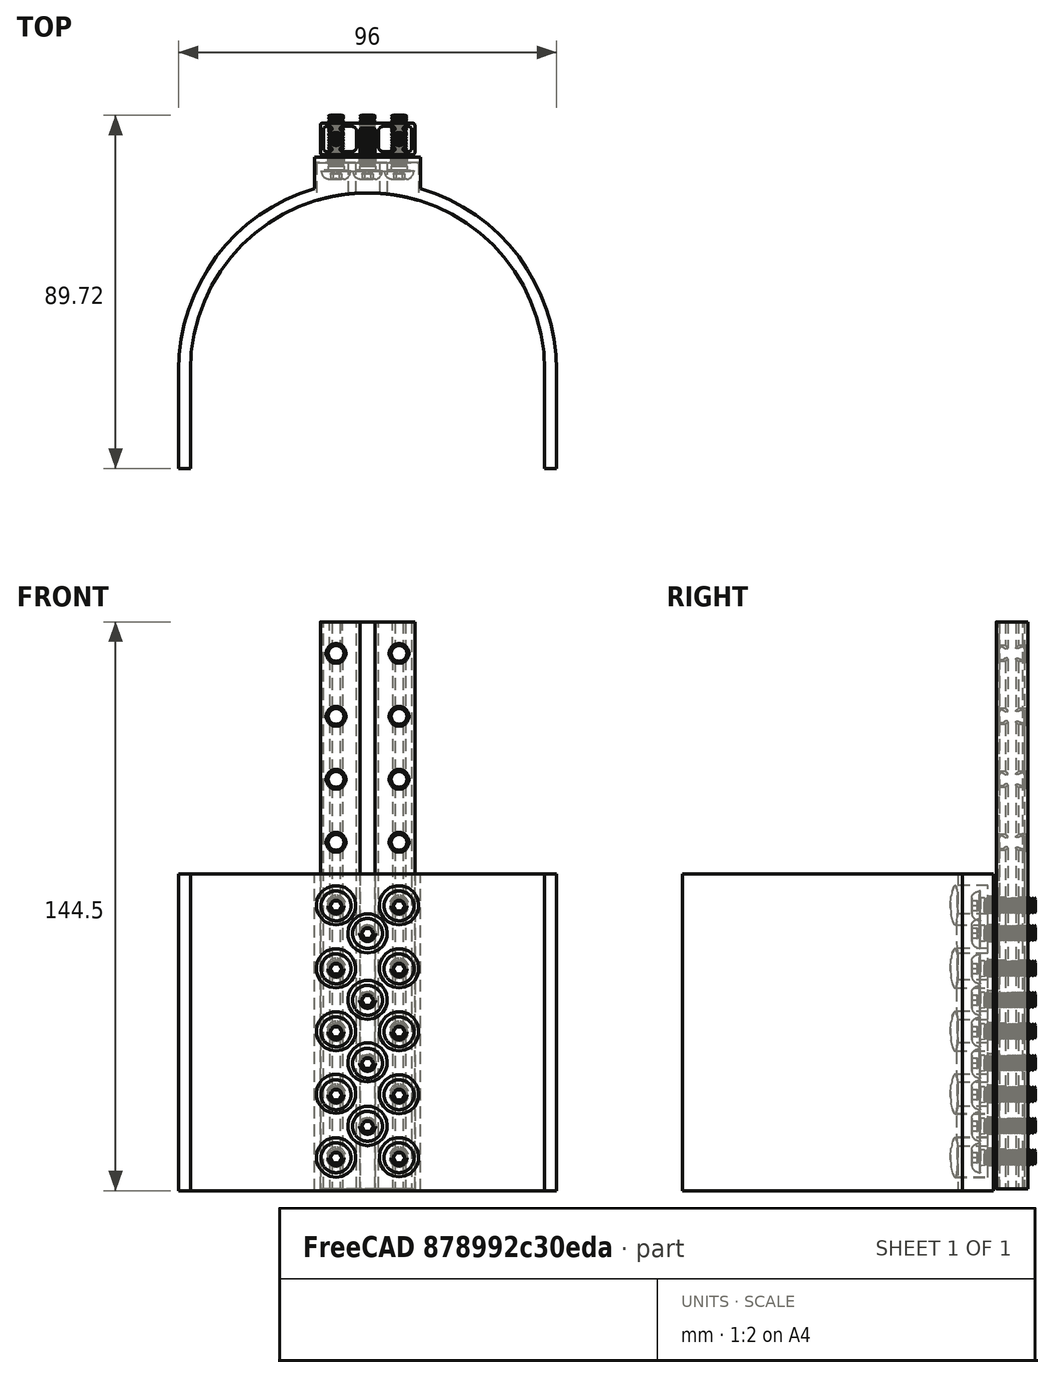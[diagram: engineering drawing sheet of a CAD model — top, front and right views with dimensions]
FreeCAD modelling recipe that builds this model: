
FCSTD DOCUMENT  (FreeCAD 0.21R33675 (Git))
Label: Mx 20223 Feeder Support v2
License: All rights reserved
LicenseURL: http://en.wikipedia.org/wiki/All_rights_reserved
objects: Part::Feature×15, Sketcher::SketchObject×3, PartDesign::Pocket×2, PartDesign::Pad×1, Mesh::Feature×1, PartDesign::Plane×1, PartDesign::Body×1
note: 26 computed .brp shape members not serialized (recipe doc carries the construction recipe); baked Part::Feature solids carry a one-line shape summary decoded from their .brp

FEATURE [Sketcher::SketchObject] Sketch
  FullyConstrained = false
  MapMode = 5
  Support = -> [XY_Plane]
  sketch-geometry (12):
    g0: LineSegment StartX=2.9811e-08 StartY=25.2897 StartZ=0 EndX=2.9811e-08 EndY=0.289669 EndZ=0
    g1: LineSegment StartX=96 StartY=25.2897 StartZ=0 EndX=96 EndY=0.289669 EndZ=0
    g2: ArcOfCircle CenterX=48 CenterY=25.2897 CenterZ=0 NormalX=0 NormalY=0 NormalZ=1 AngleXU=0 Radius=45 StartAngle=1e-16 EndAngle=3.14159
    g3: LineSegment StartX=2.9811e-08 StartY=0.289669 StartZ=0 EndX=3 EndY=0.289669 EndZ=0
    g4: LineSegment StartX=96 StartY=0.289669 StartZ=0 EndX=93 EndY=0.289669 EndZ=0
    g5: LineSegment StartX=93 StartY=25.2897 StartZ=0 EndX=93 EndY=0.289669 EndZ=0
    g6: LineSegment StartX=3 StartY=0.289669 StartZ=0 EndX=3 EndY=25.2897 EndZ=0
    g7: LineSegment StartX=34.5 StartY=79.3521 StartZ=0 EndX=61.5 EndY=79.3521 EndZ=0
    g8: LineSegment StartX=34.5 StartY=79.3521 StartZ=0 EndX=34.5 EndY=71.3521 EndZ=0
    g9: LineSegment StartX=61.5 StartY=79.3521 StartZ=0 EndX=61.5 EndY=71.3521 EndZ=0
    g10: ArcOfCircle CenterX=48 CenterY=25.2897 CenterZ=0 NormalX=0 NormalY=0 NormalZ=1 AngleXU=0 Radius=48 StartAngle=2e-16 EndAngle=1.2857
    g11: ArcOfCircle CenterX=48 CenterY=25.2897 CenterZ=0 NormalX=0 NormalY=0 NormalZ=1 AngleXU=0 Radius=48 StartAngle=1.85589 EndAngle=3.14159
  constraints (35):
    c: Vertical(g0)
    c: Vertical(g1)
    c: Equal(g0,g1)
    c: Angle(g2) = 3.14159
    c: Coincident(g3,g0)
    c: Horizontal(g3)
    c: Coincident(g4,g1)
    c: Equal(g3,g4)
    c: DistanceX(g3,g3) = 3
    c: Angle(g4,g1,g1) = 1.5708
    c: Coincident(g5,g2)
    c: Coincident(g5,g4)
    c: Coincident(g6,g3)
    c: Coincident(g6,g2)
    c: Vertical(g6)
    c: Diameter(g2) = 90
    c: DistanceY(g6,g6) = 25
    c: Equal(g6,g5)
    c: DistanceY(g0,g0) = 25
    c: Angle(g4,g5) = 1.5708
    c: DistanceY(g3,g4) = 0
    c: Horizontal(g7)
    c: DistanceX(g7,g7) = 27
    c: Coincident(g8,g7)
    c: Vertical(g8)
    c: Coincident(g9,g7)
    c: Vertical(g9)
    c: Coincident(g10,g2)
    c: Coincident(g10,g1)
    c: Coincident(g10,g9)
    c: Coincident(g11,g2)
    c: Coincident(g11,g8)
    c: Coincident(g11,g0)
    c: Equal(g8,g9)
    c: DistanceY(g8,g8) = 8
FEATURE [PartDesign::Pad] Pad
  Direction = (0,0,1)
  Length = 80.5
  Length2 = 10
  Profile = -> Sketch
  ReferenceAxis = -> Sketch [N_Axis]
  Type = 0
FEATURE [Mesh::Feature] Fantastic_Jaagub  label="ball"
  Placement = pos=(39,63,0) rot=(0,0,1;0rad)
FEATURE [Part::Feature] Part__Feature  label="Hexagon socket button head screws M4 001"
  Placement = pos=(56,90,24.5) rot=(0.01,0,0.99995;1.5708rad)
  shape: bbox 8.227 x 16.25 x 15.28 mm, 101 faces (baked)
FEATURE [Part::Feature] Part__Feature001  label="Beam0824-144˫¿؁º"
  Placement = pos=(48,88,0.5) rot=(0,0,1;3.14159rad)
  shape: bbox 24 x 8 x 144 mm, 662 faces (baked)
FEATURE [PartDesign::Plane] DatumPlane
  AttachmentOffset = pos=(0,0,14) rot=(0,1,0;3.14159rad)
  Length = 128.097
  MapMode = 45
  Placement = pos=(48,67.9376,40.25) rot=(0.57735,0.57735,-0.57735;2.0944rad)
  ResizeMode = 0
  Support = -> [Pad]
  Width = 143.597
FEATURE [Sketcher::SketchObject] Sketch001
  FullyConstrained = false
  MapMode = 5
  Placement = pos=(48,67.9376,40.25) rot=(-0.57735,-0.57735,0.57735;4.18879rad)
  Support = -> [DatumPlane]
  sketch-geometry (14):
    g0: Circle CenterX=31.8116 CenterY=-8.00605 CenterZ=0 NormalX=0 NormalY=0 NormalZ=1 AngleXU=0 Radius=5
    g1: Circle CenterX=31.7489 CenterY=7.99158 CenterZ=0 NormalX=0 NormalY=0 NormalZ=1 AngleXU=0 Radius=5
    g2: Circle CenterX=15.7464 CenterY=8.00103 CenterZ=0 NormalX=0 NormalY=0 NormalZ=1 AngleXU=0 Radius=5
    g3: Circle CenterX=15.6675 CenterY=-7.999 CenterZ=0 NormalX=0 NormalY=0 NormalZ=1 AngleXU=0 Radius=5
    g4: Circle CenterX=-0.253769 CenterY=-7.99844 CenterZ=0 NormalX=0 NormalY=0 NormalZ=1 AngleXU=0 Radius=5
    g5: Circle CenterX=-0.252174 CenterY=8.00175 CenterZ=0 NormalX=0 NormalY=0 NormalZ=1 AngleXU=0 Radius=5
    g6: Circle CenterX=-16.2562 CenterY=8.00301 CenterZ=0 NormalX=0 NormalY=0 NormalZ=1 AngleXU=0 Radius=5
    g7: Circle CenterX=-16.2572 CenterY=-8.02127 CenterZ=0 NormalX=0 NormalY=0 NormalZ=1 AngleXU=0 Radius=5
    g8: Circle CenterX=-32.2753 CenterY=-7.99234 CenterZ=0 NormalX=0 NormalY=0 NormalZ=1 AngleXU=0 Radius=5
    g9: Circle CenterX=-32.2552 CenterY=7.99149 CenterZ=0 NormalX=0 NormalY=0 NormalZ=1 AngleXU=0 Radius=5
    g10: Circle CenterX=-25.0915 CenterY=0 CenterZ=0 NormalX=0 NormalY=0 NormalZ=1 AngleXU=0 Radius=5
    g11: Circle CenterX=-8.28187 CenterY=0 CenterZ=0 NormalX=0 NormalY=0 NormalZ=1 AngleXU=0 Radius=5
    g12: Circle CenterX=7.66746 CenterY=0 CenterZ=0 NormalX=0 NormalY=0 NormalZ=1 AngleXU=0 Radius=5
    g13: Circle CenterX=23.8116 CenterY=0 CenterZ=0 NormalX=0 NormalY=0 NormalZ=1 AngleXU=0 Radius=5
  constraints (14):
    c: Diameter(g0) = 10
    c: Diameter(g1) = 10
    c: Diameter(g2) = 10
    c: Diameter(g3) = 10
    c: Diameter(g5) = 10
    c: Diameter(g4) = 10
    c: Diameter(g7) = 10
    c: Diameter(g6) = 10
    c: Diameter(g8) = 10
    c: Diameter(g9) = 10
    c: Diameter(g10) = 10
    c: Diameter(g11) = 10
    c: Diameter(g12) = 10
    c: Diameter(g13) = 10
FEATURE [Part::Feature] Part__Feature002  label="Hexagon socket button head screws M4 002"
  Placement = pos=(40,90,24.5) rot=(0.01,0,0.99995;1.5708rad)
  shape: bbox 8.227 x 16.25 x 15.28 mm, 101 faces (baked)
FEATURE [Part::Feature] Part__Feature003  label="Hexagon socket button head screws M4 003"
  Placement = pos=(56,90,40.5) rot=(0.01,0,0.99995;1.5708rad)
  shape: bbox 8.227 x 16.25 x 15.28 mm, 101 faces (baked)
FEATURE [Part::Feature] Part__Feature004  label="Hexagon socket button head screws M4 004"
  Placement = pos=(40,90,40.5) rot=(0.01,0,0.99995;1.5708rad)
  shape: bbox 8.227 x 16.25 x 15.28 mm, 101 faces (baked)
FEATURE [Part::Feature] Part__Feature005  label="Hexagon socket button head screws M4 005"
  Placement = pos=(56,90,56.5) rot=(0.01,0,0.99995;1.5708rad)
  shape: bbox 8.227 x 16.25 x 15.28 mm, 101 faces (baked)
FEATURE [Part::Feature] Part__Feature006  label="Hexagon socket button head screws M4 006"
  Placement = pos=(40,90,56.5) rot=(0.01,0,0.99995;1.5708rad)
  shape: bbox 8.227 x 16.25 x 15.28 mm, 101 faces (baked)
FEATURE [Part::Feature] Part__Feature007  label="Hexagon socket button head screws M4 007"
  Placement = pos=(56,90,72.5) rot=(0.01,0,0.99995;1.5708rad)
  shape: bbox 8.227 x 16.25 x 15.28 mm, 101 faces (baked)
FEATURE [Part::Feature] Part__Feature008  label="Hexagon socket button head screws M4 008"
  Placement = pos=(40,90,72.5) rot=(0.01,0,0.99995;1.5708rad)
  shape: bbox 8.227 x 16.25 x 15.28 mm, 101 faces (baked)
FEATURE [Part::Feature] Part__Feature009  label="Hexagon socket button head screws M4 009"
  Placement = pos=(56,90,8.5) rot=(0.01,0,0.99995;1.5708rad)
  shape: bbox 8.227 x 16.25 x 15.28 mm, 101 faces (baked)
FEATURE [Part::Feature] Part__Feature010  label="Hexagon socket button head screws M4 010"
  Placement = pos=(40,90,8.5) rot=(0.01,0,0.99995;1.5708rad)
  shape: bbox 8.227 x 16.25 x 15.28 mm, 101 faces (baked)
FEATURE [Part::Feature] Part__Feature011  label="Hexagon socket button head screws M4 011"
  Placement = pos=(48,90,16.5) rot=(0.01,0,0.99995;1.5708rad)
  shape: bbox 8.227 x 16.25 x 15.28 mm, 101 faces (baked)
FEATURE [Part::Feature] Part__Feature012  label="Hexagon socket button head screws M4 012"
  Placement = pos=(48,90,48.5) rot=(0.01,0,0.99995;1.5708rad)
  shape: bbox 8.227 x 16.25 x 15.28 mm, 101 faces (baked)
FEATURE [Part::Feature] Part__Feature013  label="Hexagon socket button head screws M4 013"
  Placement = pos=(48,90,32.5) rot=(0.01,0,0.99995;1.5708rad)
  shape: bbox 8.227 x 16.25 x 15.28 mm, 101 faces (baked)
FEATURE [Part::Feature] Part__Feature014  label="Hexagon socket button head screws M4 014"
  Placement = pos=(48,90,65.5) rot=(0.01,0,0.99995;1.5708rad)
  shape: bbox 8.227 x 16.25 x 15.28 mm, 101 faces (baked)
FEATURE [PartDesign::Pocket] Pocket
  BaseFeature = -> Pad
  Direction = (7e-16,1,-2e-16)
  Length = 10
  Length2 = 5
  Profile = -> Sketch001
  ReferenceAxis = -> Sketch001 [N_Axis]
  Type = 0
FEATURE [Sketcher::SketchObject] Sketch002
  FullyConstrained = false
  MapMode = 5
  Placement = pos=(5.52e-14,77.9376,-1.7e-14) rot=(1,0,0;1.5708rad)
  Support = -> [Pocket]
  sketch-geometry (14):
    g0: Circle CenterX=39.9938 CenterY=72.556 CenterZ=0 NormalX=0 NormalY=0 NormalZ=1 AngleXU=0 Radius=2.15
    g1: Circle CenterX=55.9997 CenterY=72.5264 CenterZ=0 NormalX=0 NormalY=0 NormalZ=1 AngleXU=0 Radius=2.15
    g2: Circle CenterX=48.0272 CenterY=65.3161 CenterZ=0 NormalX=0 NormalY=0 NormalZ=1 AngleXU=0 Radius=2.15
    g3: Circle CenterX=39.9285 CenterY=56.5172 CenterZ=0 NormalX=0 NormalY=0 NormalZ=1 AngleXU=0 Radius=2.15
    g4: Circle CenterX=55.9703 CenterY=56.467 CenterZ=0 NormalX=0 NormalY=0 NormalZ=1 AngleXU=0 Radius=2.15
    g5: Circle CenterX=47.9732 CenterY=48.561 CenterZ=0 NormalX=0 NormalY=0 NormalZ=1 AngleXU=0 Radius=2.15
    g6: Circle CenterX=39.975 CenterY=40.5071 CenterZ=0 NormalX=0 NormalY=0 NormalZ=1 AngleXU=0 Radius=2.15
    g7: Circle CenterX=55.9672 CenterY=40.5065 CenterZ=0 NormalX=0 NormalY=0 NormalZ=1 AngleXU=0 Radius=2.15
    g8: Circle CenterX=47.9704 CenterY=32.5947 CenterZ=0 NormalX=0 NormalY=0 NormalZ=1 AngleXU=0 Radius=2.15
    g9: Circle CenterX=39.9744 CenterY=24.5899 CenterZ=0 NormalX=0 NormalY=0 NormalZ=1 AngleXU=0 Radius=2.15
    g10: Circle CenterX=55.9662 CenterY=24.4989 CenterZ=0 NormalX=0 NormalY=0 NormalZ=1 AngleXU=0 Radius=2.15
    g11: Circle CenterX=47.9711 CenterY=16.4367 CenterZ=0 NormalX=0 NormalY=0 NormalZ=1 AngleXU=0 Radius=2.15
    g12: Circle CenterX=39.9238 CenterY=8.43129 CenterZ=0 NormalX=0 NormalY=0 NormalZ=1 AngleXU=0 Radius=2.15
    g13: Circle CenterX=55.967 CenterY=8.53967 CenterZ=0 NormalX=0 NormalY=0 NormalZ=1 AngleXU=0 Radius=2.15
  constraints (14):
    c: Diameter(g1) = 4.3
    c: Diameter(g11) = 4.3
    c: Diameter(g0) = 4.3
    c: Diameter(g2) = 4.3
    c: Diameter(g4) = 4.3
    c: Diameter(g3) = 4.3
    c: Diameter(g5) = 4.3
    c: Diameter(g7) = 4.3
    c: Diameter(g6) = 4.3
    c: Diameter(g8) = 4.3
    c: Diameter(g10) = 4.3
    c: Diameter(g9) = 4.3
    c: Diameter(g13) = 4.3
    c: Diameter(g12) = 4.3
FEATURE [PartDesign::Pocket] Pocket001
  BaseFeature = -> Pocket
  Direction = (7e-16,1,-2e-16)
  Length = 5
  Length2 = 5
  Profile = -> Sketch002
  ReferenceAxis = -> Sketch002 [N_Axis]
  Type = 0
FEATURE [PartDesign::Body] Body  label="Feeder-Full-Height"
  Group = -> [Sketch,Pad,DatumPlane,Sketch001,Pocket,Sketch002,Pocket001]
  Origin = -> Origin
  Tip = -> Pocket001
